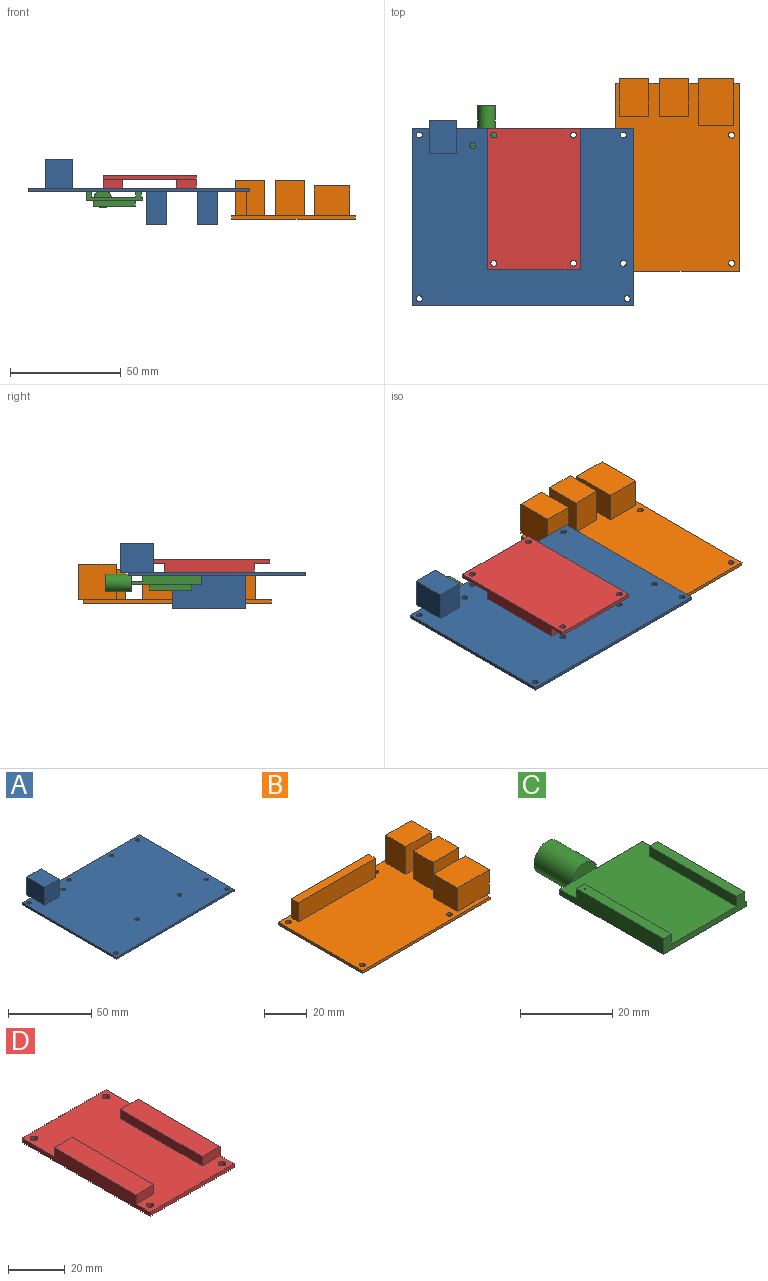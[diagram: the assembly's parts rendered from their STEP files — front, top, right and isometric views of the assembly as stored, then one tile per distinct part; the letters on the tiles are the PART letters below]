
ASSEMBLY  parts=4 mates=3
PART A: 32 faces, bbox 100x83.7x29.8 mm
  f0: plane 100x80mm, normal (0,0,-1), area 7343.3mm2, adj f2,f3,f4,f5,f6,f7,f8,f9
  f1: plane 100x80mm, normal (0,0,1), area 7802.4mm2, adj f2,f3,f4,f5,f6,f7,f8,f9
  f2: plane 100x1.5mm, normal (0,1,0), area 150mm2, adj f0,f1,f3,f5,f21
  f3: plane 80x1.5mm, normal (-1,0,0), area 120mm2, adj f0,f1,f2,f4
  f4: plane 100x1.5mm, normal (0,-1,0), area 150mm2, adj f0,f1,f3,f5
  f5: plane 80x1.5mm, normal (1,0,0), area 120mm2, adj f0,f1,f2,f4
  f6: cylinder r=1.35mm len=2.7mm, axis (0,0,1), area 12.7mm2, adj f0,f1
  f7: cylinder r=1.35mm len=2.7mm, axis (0,0,1), area 12.7mm2, adj f0,f1
  f8: cylinder r=1.35mm len=2.7mm, axis (0,0,1), area 12.7mm2, adj f0,f1
  f9: cylinder r=1.35mm len=2.7mm, axis (0,0,1), area 12.7mm2, adj f0,f1
  f10: cylinder r=1.35mm len=2.7mm, axis (0,0,1), area 12.7mm2, adj f0,f1
  f11: cylinder r=1.35mm len=2.7mm, axis (0,0,1), area 12.7mm2, adj f0,f1
  f12: cylinder r=1.35mm len=2.7mm, axis (0,0,1), area 12.7mm2, adj f0,f1
  f13: cylinder r=1.35mm len=2.7mm, axis (0,0,1), area 12.7mm2, adj f0,f1
  f14: cylinder r=1.35mm len=2.7mm, axis (0,0,1), area 12.7mm2, adj f0,f1
  f15: cylinder r=1.35mm len=2.7mm, axis (0,0,1), area 12.7mm2, adj f0,f1
  f16: plane 15.24x13.13mm, normal (1,0,0), area 200.1mm2, adj f1,f17,f19,f20,f21
  f17: plane 13.13x12.2mm, normal (0,1,0), area 160.2mm2, adj f16,f18,f20,f21
  f18: plane 15.24x13.13mm, normal (-1,0,0), area 200.1mm2, adj f1,f17,f19,f20,f21
  f19: plane 13.13x12.2mm, normal (0,-1,0), area 160.2mm2, adj f1,f16,f18,f20
  f20: plane 15.24x12.2mm, normal (0,0,1), area 185.9mm2, adj f16,f17,f18,f19
  f21: plane 12.2x3.73mm, normal (0,0,-1), area 45.5mm2, adj f2,f16,f17,f18
  f22: plane 15.15x9.11mm, normal (0,1,0), area 138mm2, adj f0,f23,f25,f26
  f23: plane 32.9x15.15mm, normal (-1,0,0), area 498.4mm2, adj f0,f22,f24,f26
  f24: plane 15.15x9.11mm, normal (0,-1,0), area 138mm2, adj f0,f23,f25,f26
  f25: plane 32.9x15.15mm, normal (1,0,0), area 498.4mm2, adj f0,f22,f24,f26
  f26: plane 32.9x9.11mm, normal (0,0,-1), area 299.7mm2, adj f22,f23,f24,f25
  f27: plane 15.15x9.11mm, normal (0,1,0), area 138mm2, adj f0,f28,f30,f31
  f28: plane 32.9x15.15mm, normal (-1,0,0), area 498.4mm2, adj f0,f27,f29,f31
  f29: plane 15.15x9.11mm, normal (0,-1,0), area 138mm2, adj f0,f28,f30,f31
  f30: plane 32.9x15.15mm, normal (1,0,0), area 498.4mm2, adj f0,f27,f29,f31
  f31: plane 32.9x9.11mm, normal (0,0,-1), area 299.7mm2, adj f27,f28,f29,f30
PART B: 33 faces, bbox 87x56x17.6 mm
  f0: plane 85x56mm, normal (0,0,1), area 3792.2mm2, adj f1,f2,f3,f4,f7,f8,f9,f12
  f1: plane 85x1.55mm, normal (0,1,0), area 131.7mm2, adj f0,f2,f4,f5
  f2: plane 56x1.55mm, normal (-1,0,0), area 86.8mm2, adj f0,f1,f3,f5
  f3: plane 85x1.55mm, normal (0,-1,0), area 131.7mm2, adj f0,f2,f4,f5
  f4: plane 56x1.55mm, normal (1,0,0), area 86.8mm2, adj f0,f1,f3,f5,f11,f17,f32
  f5: plane 85x56mm, normal (0,0,-1), area 4736.2mm2, adj f1,f2,f3,f4,f18,f19,f20,f21
  f6: plane 16x13.3mm, normal (1,0,0), area 212.8mm2, adj f7,f9,f10,f11
  f7: plane 17x16mm, normal (0,1,0), area 272mm2, adj f0,f6,f8,f10,f11
  f8: plane 16x13.3mm, normal (-1,0,0), area 212.8mm2, adj f0,f7,f9,f10
  f9: plane 17x16mm, normal (0,-1,0), area 272mm2, adj f0,f6,f8,f10,f11
  f10: plane 17x13.3mm, normal (0,0,1), area 226.1mm2, adj f6,f7,f8,f9
  f11: plane 13.3x2mm, normal (0,0,-1), area 26.6mm2, adj f4,f6,f7,f9
  f12: plane 17x16mm, normal (0,1,0), area 272mm2, adj f0,f13,f15,f16,f17
  f13: plane 16x13.3mm, normal (-1,0,0), area 212.8mm2, adj f0,f12,f14,f16
  f14: plane 17x16mm, normal (0,-1,0), area 272mm2, adj f0,f13,f15,f16,f17
  f15: plane 16x13.3mm, normal (1,0,0), area 212.8mm2, adj f12,f14,f16,f17
  f16: plane 17x13.3mm, normal (0,0,1), area 226.1mm2, adj f12,f13,f14,f15
  f17: plane 13.3x2mm, normal (0,0,-1), area 26.6mm2, adj f4,f12,f14,f15
  f18: cylinder r=1.38mm len=2.75mm, axis (0,0,1), area 13.4mm2, adj f0,f5
  f19: cylinder r=1.38mm len=2.75mm, axis (0,0,1), area 13.4mm2, adj f0,f5
  f20: cylinder r=1.38mm len=2.75mm, axis (0,0,1), area 13.4mm2, adj f0,f5
  f21: cylinder r=1.38mm len=2.75mm, axis (0,0,1), area 13.4mm2, adj f0,f5
  f22: plane 51.26x11mm, normal (0,1,0), area 563.8mm2, adj f0,f23,f25,f26
  f23: plane 11x4.64mm, normal (-1,0,0), area 51.1mm2, adj f0,f22,f24,f26
  f24: plane 51.26x11mm, normal (0,-1,0), area 563.8mm2, adj f0,f23,f25,f26
  f25: plane 11x4.64mm, normal (1,0,0), area 51.1mm2, adj f0,f22,f24,f26
  f26: plane 51.26x4.64mm, normal (0,0,1), area 237.9mm2, adj f22,f23,f24,f25
  f27: plane 21.2x13.5mm, normal (0,1,0), area 286.2mm2, adj f0,f28,f30,f31,f32
  f28: plane 16x13.5mm, normal (-1,0,0), area 216mm2, adj f0,f27,f29,f31
  f29: plane 21.2x13.5mm, normal (0,-1,0), area 286.2mm2, adj f0,f28,f30,f31,f32
  f30: plane 16x13.5mm, normal (1,0,0), area 216mm2, adj f27,f29,f31,f32
  f31: plane 21.2x16mm, normal (0,0,1), area 339.2mm2, adj f27,f28,f29,f30
  f32: plane 16x2mm, normal (0,0,-1), area 32mm2, adj f4,f27,f29,f30
PART C: 24 faces, bbox 25.4x43.2x8 mm
  f0: plane 13.97x1.5mm, normal (0,1,0), area 20.9mm2, adj f1,f5,f6,f20
  f1: plane 31.75x25.4mm, normal (0,0,1), area 672.7mm2, adj f0,f2,f3,f4,f5,f7,f8,f10
  f2: plane 3.57x1.5mm, normal (0,1,0), area 5.3mm2, adj f1,f3,f6,f20
  f3: plane 31.75x4.15mm, normal (-1,0,0), area 118.5mm2, adj f1,f2,f4,f6,f7,f9
  f4: plane 25.4x4.15mm, normal (0,-1,0), area 51.3mm2, adj f1,f3,f5,f6,f8,f9,f11,f12
  f5: plane 31.75x1.5mm, normal (1,0,0), area 47.6mm2, adj f0,f1,f4,f6
  f6: plane 31.75x25.4mm, normal (0,0,-1), area 445.4mm2, adj f0,f2,f3,f4,f5,f14,f15,f16
  f7: plane 2.65x2.5mm, normal (0,1,0), area 6.6mm2, adj f1,f3,f8,f9
  f8: plane 26.75x2.65mm, normal (1,0,0), area 70.9mm2, adj f1,f4,f7,f9
  f9: plane 26.75x2.5mm, normal (0,0,1), area 66.8mm2, adj f3,f4,f7,f8,f23
  f10: plane 2.65x2.5mm, normal (0,1,0), area 6.6mm2, adj f1,f11,f12,f13
  f11: plane 26.75x2.65mm, normal (-1,0,0), area 70.9mm2, adj f1,f4,f10,f13
  f12: plane 26.75x2.65mm, normal (1,0,0), area 70.9mm2, adj f1,f4,f10,f13
  f13: plane 26.75x2.5mm, normal (0,0,1), area 66.9mm2, adj f4,f10,f11,f12
  f14: plane 19x2.54mm, normal (0,1,0), area 48.3mm2, adj f6,f15,f17,f18
  f15: plane 19x2.54mm, normal (1,0,0), area 48.3mm2, adj f6,f14,f16,f18
  f16: plane 19x2.54mm, normal (0,-1,0), area 48.3mm2, adj f6,f15,f17,f18
  f17: plane 19x2.54mm, normal (-1,0,0), area 48.3mm2, adj f6,f14,f16,f18
  f18: plane 19x19mm, normal (0,0,-1), area 361mm2, adj f14,f15,f16,f17
  f19: plane 7.86x3.25mm, normal (0,-1,0), area 19.2mm2, adj f1,f20
  f20: cylinder r=4mm len=11.43mm, axis (0,-1,0), area 287.3mm2, adj f0,f2,f19,f21,f22
  f21: plane 8x8mm, normal (0,1,0), area 50.3mm2, adj f20
  f22: plane 7.86x3.25mm, normal (0,-1,0), area 19.2mm2, adj f6,f20
  f23: cylinder r=0.15mm len=4.15mm, axis (0,0,1), area 3.9mm2, adj f6,f9
PART D: 18 faces, bbox 42x64x5.8 mm
  f0: plane 64x42mm, normal (0,0,1), area 1937.4mm2, adj f1,f2,f3,f4,f6,f7,f8,f9
  f1: plane 42x1.75mm, normal (0,1,0), area 73.6mm2, adj f0,f2,f4,f5
  f2: plane 64x5.75mm, normal (-1,0,0), area 275.6mm2, adj f0,f1,f3,f5,f10,f11,f13
  f3: plane 42x1.75mm, normal (0,-1,0), area 73.6mm2, adj f0,f2,f4,f5
  f4: plane 64x5.75mm, normal (1,0,0), area 275.8mm2, adj f0,f1,f3,f5,f14,f16,f17
  f5: plane 64x42mm, normal (0,0,-1), area 2665.1mm2, adj f1,f2,f3,f4,f6,f7,f8,f9
  f6: cylinder r=1.35mm len=2.7mm, axis (0,0,-1), area 14.9mm2, adj f0,f5
  f7: cylinder r=1.35mm len=2.7mm, axis (0,0,-1), area 14.9mm2, adj f0,f5
  f8: cylinder r=1.35mm len=2.7mm, axis (0,0,-1), area 14.9mm2, adj f0,f5
  f9: cylinder r=1.35mm len=2.7mm, axis (0,0,-1), area 14.9mm2, adj f0,f5
  f10: plane 8.9x4mm, normal (0,1,0), area 35.6mm2, adj f0,f2,f12,f13
  f11: plane 8.9x4mm, normal (0,-1,0), area 35.6mm2, adj f0,f2,f12,f13
  f12: plane 40.86x4mm, normal (1,0,0), area 163.5mm2, adj f0,f10,f11,f13
  f13: plane 40.86x8.9mm, normal (0,0,1), area 363.7mm2, adj f2,f10,f11,f12
  f14: plane 8.9x4mm, normal (0,1,0), area 35.6mm2, adj f0,f4,f15,f17
  f15: plane 40.9x4mm, normal (-1,0,0), area 163.6mm2, adj f0,f14,f16,f17
  f16: plane 8.9x4mm, normal (0,-1,0), area 35.6mm2, adj f0,f4,f15,f17
  f17: plane 40.9x8.9mm, normal (0,0,1), area 364mm2, adj f4,f14,f15,f16
PLACE A rot(axis=(0.88,0.48,0.05),0deg) t=(-17.84,13.57,8.45)mm
PLACE B rot(axis=(0,0,1),90deg) t=(12.01,33.25,-4.1)mm
PLACE C rot(axis=(0.88,0.48,0.05),0deg) t=(-32.36,35.45,4.3)mm
PLACE D rot(axis=(0,-1,0),180deg) t=(-15.03,18.61,15.71)mm
MATE fastened C.f23 <-> A.f7  axis (0,0,1) through (-43.3,42.93,8.45)mm
MATE fastened A.f10 <-> D.f8  axis (0,0,1) through (2.2,-10.3,9.95)mm
MATE fastened B.f18 <-> A.f9  axis (0,0,1) through (24.7,-10.3,-2.55)mm
